# Revit family: Deca_Válvula de escoamento para lavatório cuba e bidê_Válvula Escoamento Luxo_1601
name_source: partatom
category: Plumbing Fixtures
units: mm (PartAtom-declared; Revit-internal decimal feet)

## family parameters
Cut with Voids When Loaded = No
Host = Face
Part Type = Normal
Room Calculation Point = No
Round Connector Dimension = Use Radius
Shared = No

## types (7) — shared parameters
Acompanha o Produto = -
Aprovado por = quattroD
Atendimento ao Cliente = 0800-0117073
Categoria = COMPLEMENTARES
Composição Anel Vedação = -
Composição Assento = -
Composição Básica = Liga de Cobre (bronze e latão),Plásticos de Engenharia,Elastômeros
Composição Componente = -
Consumo = -
Cor Interna = -
Cor Secundária = -
Cores Componente = -
Criado por = quattroD
Código Pai = 1601
Description = Válvula de escoamento para lavatório cuba e bidê
Diâmetro Ponto de Esgoto = 25 mm  [stored 0.082021 ft]
Informações Complementares = -
Itens de Instalação = -
Linha = Válvula Escoamento Luxo
Manufacturer = Deca
Norma = NBR15423
Peso Líquido (Kg) = 0.094
Pressão máx. funcionamento = -
Pressão mín. Aquec. Acúmulo = -
Pressão mín. Aquec. Passagem = -
Pressão mín. funcionamento = -
Raio Ponto de Esgoto = 13 mm
Saída de Esgoto = -
Segmento = Banheiro Luxo
Tipo de dispositivo economizador = -
Tipo de mecanismo utilizado = -
Tipo de rosca de entrada = -
Tipo de rosca de saída = BSP NBR 8133
URL = www.deca.com.br
Vazão na Pressão máx. (L/min) = -
Vazão na Pressão mín. (L/min) = -
zero-valued in all types: CWFU, Default Elevation, WFU

## per-type parameters (varying)
| type | Cor Principal | Material | Model |
| 1601.C_Cromado | Cromado | Deca_Cromado | 1601.C |
| 1601.BL.NO_Black Noir | Black Noir | Deca_Black Noir | 1601.BL.NO |
| 1601.GL_Gold | Gold | Deca_Gold | 1601.GL |
| 1601.CT.MT_Corten | Corten | Deca_Corten | 1601.CT.MT |
| 1601.GL.RD_Red Gold | Red Gold | Deca_Red Gold | 1601.GL.RD |
| 1601.GL.MT_Gold Matte | Gold Matte | Deca_Gold Matte | 1601.GL.MT |
| 1601.BL.MT_Black Matte | Black Matte | Deca_Black Matte | 1601.BL.MT |

note: [stored X ft] marks values corroborated as IEEE doubles in the binary element streams (Revit-internal decimal feet)

## geometry (parser evidence)
native form markers: Sweep x2
no freeform markers — native parametric forms only
